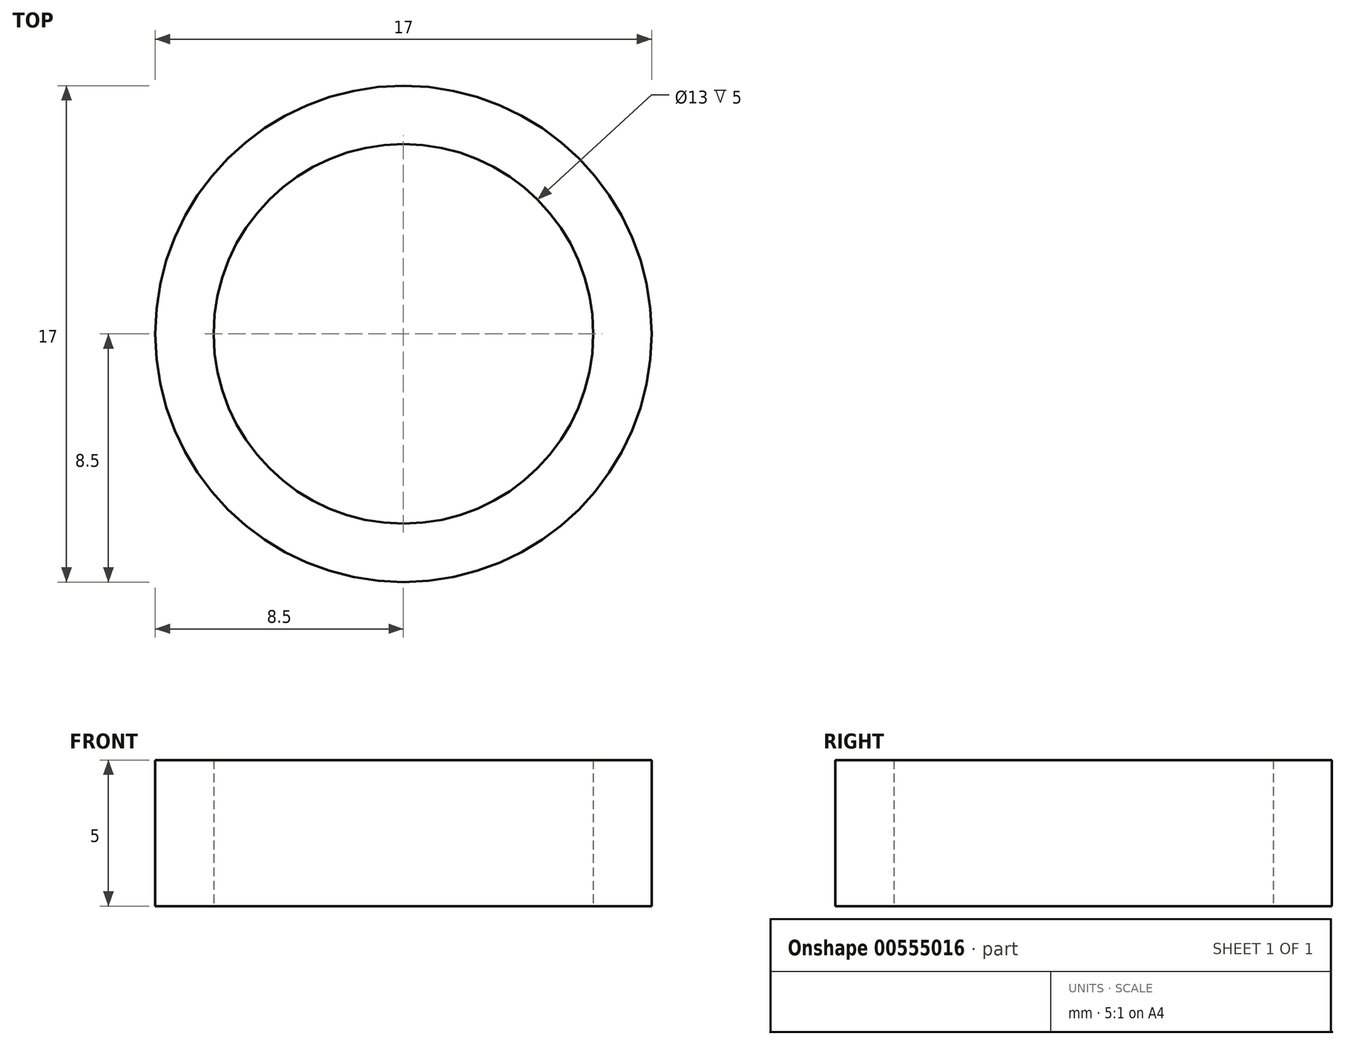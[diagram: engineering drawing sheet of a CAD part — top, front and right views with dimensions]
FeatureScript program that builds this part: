
annotation { "Feature Type Name" : "Feature", "Feature Type Description" : "" }
export const myFeature = defineFeature(function(context is Context, id is Id, definition is map)
    precondition{}
    {
        {
            var Q0;
            Q0=qCreatedBy(makeId("Top.planeOp"),FACE);
            var sketch = newSketch(context, id + "F0", { "sketchPlane" : qUnion([Q0])});
            skCircle(sketch, "E0", {"center": v(0, 0) * mm, "radius": 8.5 * mm});
            skCircle(sketch, "E1", {"center": v(0, 0) * mm, "radius": 6.5 * mm});
            skSolve(sketch);
        }
        {
            var Q0;
            Q0=makeQuery(id+"F0.imprint","IMPRINT",FACE,{"disambiguationData":[TD([[makeQuery(id+"F0.imprint","IMPRINT",EDGE,{"derivedFrom":sQuery(id+"F0.wireOp",EDGE,"E0")}),1.0]])]});
            extrude(context, id + "F1", {"entities" : qUnion([Q0]), "depth" : 5 * mm, "offsetDistance" : 25 * mm});
        }
    });
